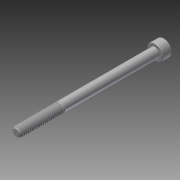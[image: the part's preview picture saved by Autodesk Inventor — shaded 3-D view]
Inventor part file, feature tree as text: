
AUTODESK INVENTOR PART (.ipt)
format: ipt  version: 2014 SP1 (Build 180222100, 222)  size: 524,288 bytes
history: native  units: in
note: dims shown in document units (in); Inventor stores cm internally (conversion verified against a paired STEP export)
features: chamfer x1, other x1, imported_body x1
ambient origin geometry x8: Origin, YZ Plane, XZ Plane, XY Plane, X Axis, Y Axis, Z Axis, Center Point
bodies: Body1 (feature_tree)
feature tree (3):
  chamfer  "Chamfer2"  [1 undecoded]
  other  "91251A2561"
  imported_body  "Base1"
note: 1 required parameter value undecoded (feature->parameter linkage not recoverable at this tier; creation-order binding heuristic only, values carry confidence <= 0.55)
